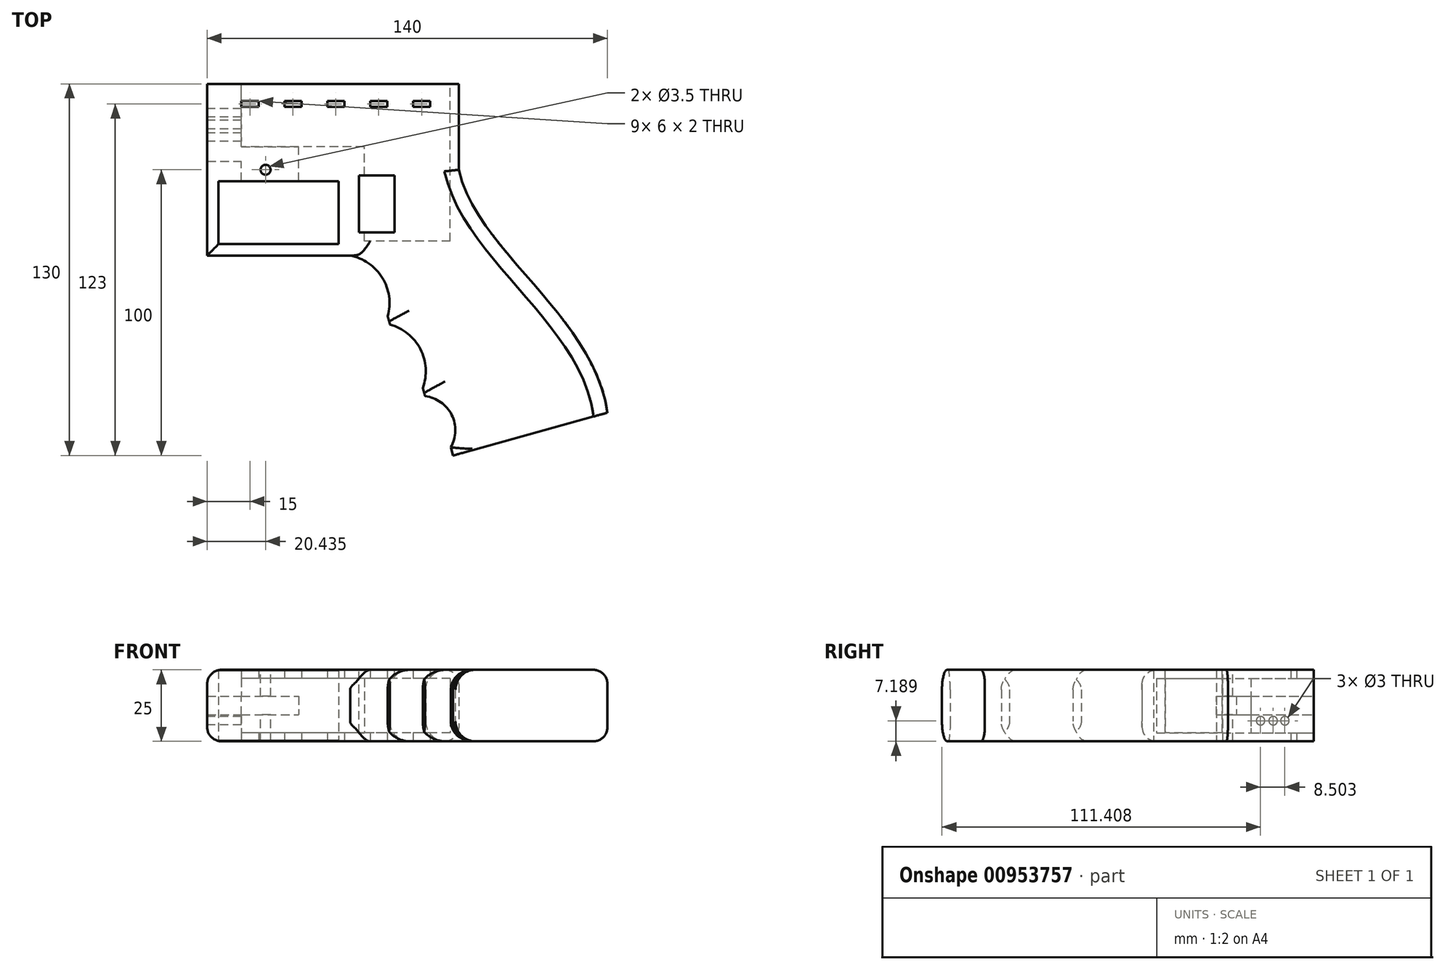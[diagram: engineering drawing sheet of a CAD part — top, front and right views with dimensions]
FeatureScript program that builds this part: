
annotation { "Feature Type Name" : "Feature", "Feature Type Description" : "" }
export const myFeature = defineFeature(function(context is Context, id is Id, definition is map)
    precondition{}
    {
        {
            var Q0;
            Q0=qCreatedBy(makeId("Top.planeOp"),FACE);
            var sketch = newSketch(context, id + "F0", { "sketchPlane" : qUnion([Q0])});
            skLineSegment(sketch, "E0.bottom", {"start": v(-44, 30) * mm, "end": v(44, 30) * mm});
            skLineSegment(sketch, "E0.top", {"start": v(-44, -30) * mm, "end": v(44, -30) * mm});
            skLineSegment(sketch, "E0.left", {"start": v(-44, 30) * mm, "end": v(-44, -30) * mm});
            skLineSegment(sketch, "E0.right", {"start": v(44, 30) * mm, "end": v(44, -30) * mm});
            skPoint(sketch, "E0.middle", {"position": v(0, 0) * mm});
            skLineSegment(sketch, "E1.bottom", {"start": v(-40, -4) * mm, "end": v(2, -4) * mm});
            skLineSegment(sketch, "E1.top", {"start": v(-40, -26) * mm, "end": v(2, -26) * mm});
            skLineSegment(sketch, "E1.left", {"start": v(-40, -4) * mm, "end": v(-40, -26) * mm});
            skLineSegment(sketch, "E1.right", {"start": v(2, -4) * mm, "end": v(2, -26) * mm});
            skLineSegment(sketch, "E2.bottom", {"start": v(-32, 24) * mm, "end": v(-26, 24) * mm});
            skLineSegment(sketch, "E2.top", {"start": v(-32, 22) * mm, "end": v(-26, 22) * mm});
            skLineSegment(sketch, "E2.left", {"start": v(-32, 24) * mm, "end": v(-32, 22) * mm});
            skLineSegment(sketch, "E2.right", {"start": v(-26, 24) * mm, "end": v(-26, 22) * mm});
            skLineSegment(sketch, "E3.1.0.0", {"start": v(-17, 24) * mm, "end": v(-11, 24) * mm});
            skLineSegment(sketch, "E3.1.0.1", {"start": v(-17, 22) * mm, "end": v(-11, 22) * mm});
            skLineSegment(sketch, "E3.1.0.2", {"start": v(-11, 24) * mm, "end": v(-11, 22) * mm});
            skLineSegment(sketch, "E3.1.0.3", {"start": v(-17, 24) * mm, "end": v(-17, 22) * mm});
            skLineSegment(sketch, "E3.2.0.0", {"start": v(-2, 24) * mm, "end": v(4, 24) * mm});
            skLineSegment(sketch, "E3.2.0.1", {"start": v(-2, 22) * mm, "end": v(4, 22) * mm});
            skLineSegment(sketch, "E3.2.0.2", {"start": v(4, 24) * mm, "end": v(4, 22) * mm});
            skLineSegment(sketch, "E3.2.0.3", {"start": v(-2, 24) * mm, "end": v(-2, 22) * mm});
            skLineSegment(sketch, "E3.direction1", {"start": v(-32, 22) * mm, "end": v(-17, 22) * mm, "construction": true});
            skLineSegment(sketch, "E4.0.3.0", {"start": v(13, 24) * mm, "end": v(19, 24) * mm});
            skLineSegment(sketch, "E4.3.3.0", {"start": v(13, 22) * mm, "end": v(19, 22) * mm});
            skLineSegment(sketch, "E4.6.3.0", {"start": v(19, 24) * mm, "end": v(19, 22) * mm});
            skLineSegment(sketch, "E4.9.3.0", {"start": v(13, 24) * mm, "end": v(13, 22) * mm});
            skLineSegment(sketch, "E4.0.4.0", {"start": v(28, 24) * mm, "end": v(34, 24) * mm});
            skLineSegment(sketch, "E4.3.4.0", {"start": v(28, 22) * mm, "end": v(34, 22) * mm});
            skLineSegment(sketch, "E4.6.4.0", {"start": v(34, 24) * mm, "end": v(34, 22) * mm});
            skLineSegment(sketch, "E4.9.4.0", {"start": v(28, 24) * mm, "end": v(28, 22) * mm});
            skFitSpline(sketch, "E5", {"points": [v(44, 0) * mm, v(96, -85) * mm], "startDerivative": vector(19.3, -85.84) * mm, "endDerivative": vector(14.65, -101.93) * mm});
            skLineSegment(sketch, "E6", {"start": v(96, -85) * mm, "end": v(42.05, -100) * mm});
            skLineSegment(sketch, "E7", {"start": v(42.05, -100) * mm, "end": v(41.24, -97.1) * mm});
            skArc(sketch, "E8", {"start": v(41.24, -97.1) * mm, "mid": v(41.53, -85.76) * mm, "end": v(32.23, -79.26) * mm});
            skLineSegment(sketch, "E9", {"start": v(32.23, -79.26) * mm, "end": v(31.42, -76.37) * mm});
            skArc(sketch, "E10", {"start": v(31.42, -76.37) * mm, "mid": v(30.55, -62.75) * mm, "end": v(19.95, -54.16) * mm});
            skLineSegment(sketch, "E11", {"start": v(19.95, -54.16) * mm, "end": v(19.14, -51.27) * mm});
            skArc(sketch, "E12", {"start": v(19.14, -51.27) * mm, "mid": v(17.23, -37.75) * mm, "end": v(6, -30) * mm});
            skSolve(sketch);
        }
        {
            var Q0;
            {var subQ5=sQuery(id+"F0.wireOp",EDGE,"E0.bottom");Q0=makeQuery(id+"F0.imprint","IMPRINT",FACE,{"disambiguationData":[TD([[makeQuery(id+"F0.imprint","IMPRINT",EDGE,{"derivedFrom":subQ5}),-1.0]])]});}
            var Q1;
            {var subQ0=sQuery(id+"F0.wireOp",EDGE,"E5");Q1=makeQuery(id+"F0.imprint","IMPRINT",FACE,{"disambiguationData":[TD([[makeQuery(id+"F0.imprint","IMPRINT",EDGE,{"derivedFrom":subQ0}),-1.0]])]});}
            extrude(context, id + "F1", {"entities" : qUnion([Q0, Q1]), "depth" : 25 * mm, "offsetDistance" : 25 * mm});
        }
        {
            var Q0;
            Q0=makeQuery(id+"F1.opExtrude","SWEPT_FACE",FACE,{"disambiguationData":[OSD([sQuery(id+"F0.wireOp",EDGE,"E0.bottom")])]});
            var sketch = newSketch(context, id + "F2", { "sketchPlane" : qUnion([Q0])});
            skLineSegment(sketch, "E13.bottom", {"start": v(-41, 22) * mm, "end": v(32, 22) * mm});
            skLineSegment(sketch, "E13.top", {"start": v(-41, 3) * mm, "end": v(32, 3) * mm});
            skLineSegment(sketch, "E13.left", {"start": v(-41, 22) * mm, "end": v(-41, 3) * mm});
            skLineSegment(sketch, "E13.right", {"start": v(32, 22) * mm, "end": v(32, 3) * mm});
            skLineSegment(sketch, "E14", {"start": v(-11, 22) * mm, "end": v(-11, 3) * mm});
            skLineSegment(sketch, "E15.bottom", {"start": v(44, 15.75) * mm, "end": v(12, 15.75) * mm});
            skLineSegment(sketch, "E15.top", {"start": v(44, 9.25) * mm, "end": v(12, 9.25) * mm});
            skLineSegment(sketch, "E15.left", {"start": v(44, 15.75) * mm, "end": v(44, 9.25) * mm});
            skLineSegment(sketch, "E15.right", {"start": v(12, 15.75) * mm, "end": v(12, 9.25) * mm});
            skLineSegment(sketch, "E16", {"start": v(25.85, 15.75) * mm, "end": v(25.85, 22) * mm, "construction": true});
            skLineSegment(sketch, "E17", {"start": v(25.61, 9.25) * mm, "end": v(25.61, 3) * mm, "construction": true});
            skSolve(sketch);
        }
        {
            var Q0;
            {var subQ0=sQuery(id+"F2.wireOp",EDGE,"E13.left");Q0=makeQuery(id+"F2.imprint","IMPRINT",FACE,{"disambiguationData":[TD([[makeQuery(id+"F2.imprint","IMPRINT",EDGE,{"derivedFrom":subQ0}),1.0]])]});}
            var Q1;
            {var subQ9=sQuery(id+"F2.wireOp",EDGE,"E14");Q1=makeQuery(id+"F2.imprint","IMPRINT",FACE,{"disambiguationData":[TD([[makeQuery(id+"F2.imprint","IMPRINT",EDGE,{"derivedFrom":subQ9}),1.0]])]});}
            var Q2;
            {var subQ5=sQuery(id+"F2.wireOp",EDGE,"E15.right");Q2=makeQuery(id+"F2.imprint","IMPRINT",FACE,{"disambiguationData":[TD([[makeQuery(id+"F2.imprint","IMPRINT",EDGE,{"derivedFrom":subQ5}),1.0]])]});}
            var Q3;
            {var subQ5=sQuery(id+"F2.wireOp",EDGE,"E15.left");Q3=makeQuery(id+"F2.imprint","IMPRINT",FACE,{"disambiguationData":[TD([[makeQuery(id+"F2.imprint","IMPRINT",EDGE,{"derivedFrom":subQ5}),-1.0]])]});}
            extrude(context, id + "F3", {"entities" : qUnion([Q0, Q1, Q2, Q3]), "operationType" : NewBodyOperationType.REMOVE, "oppositeDirection" : true, "depth" : 22 * mm, "offsetDistance" : 25 * mm});
        }
        {
            var Q0;
            {var subQ0=sQuery(id+"F2.wireOp",EDGE,"E13.left");Q0=makeQuery(id+"F2.imprint","IMPRINT",FACE,{"disambiguationData":[TD([[makeQuery(id+"F2.imprint","IMPRINT",EDGE,{"derivedFrom":subQ0}),1.0]])]});}
            extrude(context, id + "F4", {"entities" : qUnion([Q0]), "operationType" : NewBodyOperationType.REMOVE, "oppositeDirection" : true, "depth" : 55 * mm, "offsetDistance" : 25 * mm});
        }
        {
            var Q0;
            {var subQ5=sQuery(id+"F2.wireOp",EDGE,"E15.right");Q0=makeQuery(id+"F2.imprint","IMPRINT",FACE,{"disambiguationData":[TD([[makeQuery(id+"F2.imprint","IMPRINT",EDGE,{"derivedFrom":subQ5}),1.0]])]});}
            var Q1;
            Q1=makeQuery(id+"F1.opExtrude","SWEPT_FACE",FACE,{"disambiguationData":[OSD([sQuery(id+"F0.wireOp",EDGE,"E1.bottom")])]});
            extrude(context, id + "F5", {"entities" : qUnion([Q0]), "operationType" : NewBodyOperationType.REMOVE, "endBound" : BoundingType.UP_TO_SURFACE, "oppositeDirection" : true, "depth" : 25 * mm, "endBoundEntityFace" : qUnion([Q1]), "offsetDistance" : 25 * mm});
        }
        {
            var Q0;
            {var subQ5=sQuery(id+"F2.wireOp",EDGE,"E15.left");Q0=makeQuery(id+"F2.imprint","IMPRINT",FACE,{"disambiguationData":[TD([[makeQuery(id+"F2.imprint","IMPRINT",EDGE,{"derivedFrom":subQ5}),-1.0]])]});}
            extrude(context, id + "F6", {"entities" : qUnion([Q0]), "operationType" : NewBodyOperationType.REMOVE, "oppositeDirection" : true, "depth" : 27 * mm, "offsetDistance" : 25 * mm});
        }
        {
            var Q0;
            Q0=makeQuery(id+"F1.opExtrude","CAP_EDGE",EDGE,{"disambiguationData":[OSD([sQuery(id+"F0.wireOp",EDGE,"E11")])],"isStart":false});
            var Q1;
            Q1=makeQuery(id+"F1.opExtrude","CAP_EDGE",EDGE,{"disambiguationData":[OSD([sQuery(id+"F0.wireOp",EDGE,"E12")])],"isStart":false});
            var Q2;
            Q2=makeQuery(id+"F1.opExtrude","CAP_EDGE",EDGE,{"disambiguationData":[OSD([sQuery(id+"F0.wireOp",EDGE,"E10")])],"isStart":false});
            var Q3;
            Q3=makeQuery(id+"F1.opExtrude","CAP_EDGE",EDGE,{"disambiguationData":[OSD([sQuery(id+"F0.wireOp",EDGE,"E9")])],"isStart":false});
            var Q4;
            Q4=makeQuery(id+"F1.opExtrude","CAP_EDGE",EDGE,{"disambiguationData":[OSD([sQuery(id+"F0.wireOp",EDGE,"E8")])],"isStart":false});
            var Q5;
            Q5=makeQuery(id+"F1.opExtrude","CAP_EDGE",EDGE,{"disambiguationData":[OSD([sQuery(id+"F0.wireOp",EDGE,"E7")])],"isStart":false});
            fillet(context, id + "F7", {"entities" : qUnion([Q0, Q1, Q2, Q3, Q4, Q5]), "radius" : 7 * mm, "tangentPropagation" : true, "allowEdgeOverflow" : false});
        }
        {
            var Q0;
            Q0=makeQuery(id+"F1.opExtrude","CAP_EDGE",EDGE,{"disambiguationData":[OSD([sQuery(id+"F0.wireOp",EDGE,"E12")])],"isStart":true});
            var Q1;
            Q1=makeQuery(id+"F1.opExtrude","CAP_EDGE",EDGE,{"disambiguationData":[OSD([sQuery(id+"F0.wireOp",EDGE,"E11")])],"isStart":true});
            var Q2;
            Q2=makeQuery(id+"F1.opExtrude","CAP_EDGE",EDGE,{"disambiguationData":[OSD([sQuery(id+"F0.wireOp",EDGE,"E10")])],"isStart":true});
            var Q3;
            Q3=makeQuery(id+"F1.opExtrude","CAP_EDGE",EDGE,{"disambiguationData":[OSD([sQuery(id+"F0.wireOp",EDGE,"E9")])],"isStart":true});
            var Q4;
            Q4=makeQuery(id+"F1.opExtrude","CAP_EDGE",EDGE,{"disambiguationData":[OSD([sQuery(id+"F0.wireOp",EDGE,"E8")])],"isStart":true});
            var Q5;
            Q5=makeQuery(id+"F1.opExtrude","CAP_EDGE",EDGE,{"disambiguationData":[OSD([sQuery(id+"F0.wireOp",EDGE,"E7")])],"isStart":true});
            fillet(context, id + "F8", {"entities" : qUnion([Q0, Q1, Q2, Q3, Q4, Q5]), "radius" : 7 * mm, "tangentPropagation" : true, "allowEdgeOverflow" : false});
        }
        {
            var Q0;
            Q0=makeQuery(id+"F1.opExtrude","CAP_EDGE",EDGE,{"disambiguationData":[OSD([sQuery(id+"F0.wireOp",EDGE,"E0.left")])],"isStart":false});
            var Q1;
            Q1=makeQuery(id+"F1.opExtrude","CAP_EDGE",EDGE,{"disambiguationData":[OSD([sQuery(id+"F0.wireOp",EDGE,"E0.top")])],"isStart":false});
            var Q2;
            Q2=makeQuery(id+"F1.opExtrude","CAP_EDGE",EDGE,{"disambiguationData":[OSD([sQuery(id+"F0.wireOp",EDGE,"E0.right")])],"isStart":false});
            var Q3;
            Q3=makeQuery(id+"F1.opExtrude","CAP_EDGE",EDGE,{"disambiguationData":[OSD([sQuery(id+"F0.wireOp",EDGE,"E5")])],"isStart":false});
            var Q4;
            Q4=makeQuery(id+"F1.opExtrude","CAP_EDGE",EDGE,{"disambiguationData":[OSD([sQuery(id+"F0.wireOp",EDGE,"E5")])],"isStart":true});
            var Q5;
            Q5=makeQuery(id+"F1.opExtrude","CAP_EDGE",EDGE,{"disambiguationData":[OSD([sQuery(id+"F0.wireOp",EDGE,"E0.right")])],"isStart":true});
            var Q6;
            Q6=makeQuery(id+"F1.opExtrude","CAP_EDGE",EDGE,{"disambiguationData":[OSD([sQuery(id+"F0.wireOp",EDGE,"E0.left")])],"isStart":true});
            var Q7;
            Q7=makeQuery(id+"F1.opExtrude","CAP_EDGE",EDGE,{"disambiguationData":[OSD([sQuery(id+"F0.wireOp",EDGE,"E0.top")])],"isStart":true});
            fillet(context, id + "F9", {"entities" : qUnion([Q0, Q1, Q2, Q3, Q4, Q5, Q6, Q7]), "radius" : 5 * mm, "tangentPropagation" : true, "allowEdgeOverflow" : false});
        }
        {
            var Q0;
            Q0=makeQuery(id+"F1.opExtrude","CAP_FACE",FACE,{"disambiguationData":[OSD([sQuery(id+"F0.wireOp",EDGE,"E0.bottom"),sQuery(id+"F0.wireOp",EDGE,"E0.top"),sQuery(id+"F0.wireOp",EDGE,"E0.left"),sQuery(id+"F0.wireOp",EDGE,"E0.right"),sQuery(id+"F0.wireOp",EDGE,"E1.bottom"),sQuery(id+"F0.wireOp",EDGE,"E1.top"),sQuery(id+"F0.wireOp",EDGE,"E1.left"),sQuery(id+"F0.wireOp",EDGE,"E1.right"),sQuery(id+"F0.wireOp",EDGE,"E2.bottom"),sQuery(id+"F0.wireOp",EDGE,"E2.top"),sQuery(id+"F0.wireOp",EDGE,"E2.left"),sQuery(id+"F0.wireOp",EDGE,"E2.right"),sQuery(id+"F0.wireOp",EDGE,"E3.1.0.0"),sQuery(id+"F0.wireOp",EDGE,"E3.1.0.1"),sQuery(id+"F0.wireOp",EDGE,"E3.1.0.2"),sQuery(id+"F0.wireOp",EDGE,"E3.1.0.3"),sQuery(id+"F0.wireOp",EDGE,"E3.2.0.0"),sQuery(id+"F0.wireOp",EDGE,"E3.2.0.1"),sQuery(id+"F0.wireOp",EDGE,"E3.2.0.2"),sQuery(id+"F0.wireOp",EDGE,"E3.2.0.3"),sQuery(id+"F0.wireOp",EDGE,"E4.0.3.0"),sQuery(id+"F0.wireOp",EDGE,"E4.3.3.0"),sQuery(id+"F0.wireOp",EDGE,"E4.6.3.0"),sQuery(id+"F0.wireOp",EDGE,"E4.9.3.0"),sQuery(id+"F0.wireOp",EDGE,"E4.0.4.0"),sQuery(id+"F0.wireOp",EDGE,"E4.3.4.0"),sQuery(id+"F0.wireOp",EDGE,"E4.6.4.0"),sQuery(id+"F0.wireOp",EDGE,"E4.9.4.0"),sQuery(id+"F0.wireOp",EDGE,"E5"),sQuery(id+"F0.wireOp",EDGE,"E6"),sQuery(id+"F0.wireOp",EDGE,"E7"),sQuery(id+"F0.wireOp",EDGE,"E8"),sQuery(id+"F0.wireOp",EDGE,"E9"),sQuery(id+"F0.wireOp",EDGE,"E10"),sQuery(id+"F0.wireOp",EDGE,"E11"),sQuery(id+"F0.wireOp",EDGE,"E12")])],"isStart":false});
            var sketch = newSketch(context, id + "F10", { "sketchPlane" : qUnion([Q0])});
            skCircle(sketch, "E18", {"center": v(-23.57, 0) * mm, "radius": 1.75 * mm});
            skSolve(sketch);
        }
        {
            var Q0;
            Q0=makeQuery(id+"F10.imprint","IMPRINT",FACE,{"disambiguationData":[TD([[makeQuery(id+"F10.imprint","IMPRINT",EDGE,{"derivedFrom":sQuery(id+"F10.wireOp",EDGE,"E18")}),1.0]])]});
            extrude(context, id + "F11", {"entities" : qUnion([Q0]), "operationType" : NewBodyOperationType.REMOVE, "endBound" : BoundingType.THROUGH_ALL, "oppositeDirection" : true, "depth" : 25 * mm, "offsetDistance" : 25 * mm});
        }
        {
            var Q0;
            Q0=makeQuery(id+"F1.opExtrude","SWEPT_FACE",FACE,{"disambiguationData":[OSD([sQuery(id+"F0.wireOp",EDGE,"E0.left")])]});
            var sketch = newSketch(context, id + "F12", { "sketchPlane" : qUnion([Q0])});
            skCircle(sketch, "E19", {"center": v(-19.91, 7.19) * mm, "radius": 1.5 * mm});
            skCircle(sketch, "E20", {"center": v(-15.82, 7.19) * mm, "radius": 1.5 * mm});
            skCircle(sketch, "E21", {"center": v(-11.4, 7.19) * mm, "radius": 1.5 * mm});
            skSolve(sketch);
        }
        {
            var Q0;
            Q0 = qSketchRegion(id + "F12", true);
            extrude(context, id + "F13", {"entities" : qUnion([Q0]), "operationType" : NewBodyOperationType.REMOVE, "endBound" : BoundingType.UP_TO_NEXT, "oppositeDirection" : true, "depth" : 25 * mm, "offsetDistance" : 25 * mm});
        }
        {
            var Q0;
            Q0=makeQuery(id+"F10.imprint","IMPRINT",FACE,{"disambiguationData":[TD([[makeQuery(id+"F10.imprint","IMPRINT",EDGE,{"derivedFrom":sQuery(id+"F10.wireOp",EDGE,"E18")}),-1.0]])]});
            var Q1;
            Q1=makeQuery(id+"F10.imprint","IMPRINT",FACE,{"disambiguationData":[TD([[makeQuery(id+"F10.imprint","IMPRINT",EDGE,{"derivedFrom":sQuery(id+"F10.wireOp",EDGE,"E18")}),-1.0]])]});
            var sketch = newSketch(context, id + "F14", { "sketchPlane" : qUnion([Q0, Q1])});
            skLineSegment(sketch, "E22.bottom", {"start": v(9.09, -1.98) * mm, "end": v(21.59, -1.98) * mm});
            skLineSegment(sketch, "E22.top", {"start": v(9.09, -21.98) * mm, "end": v(21.59, -21.98) * mm});
            skLineSegment(sketch, "E22.left", {"start": v(9.09, -1.98) * mm, "end": v(9.09, -21.98) * mm});
            skLineSegment(sketch, "E22.right", {"start": v(21.59, -1.98) * mm, "end": v(21.59, -21.98) * mm});
            skSolve(sketch);
        }
        {
            var Q0;
            Q0 = qSketchRegion(id + "F14", true);
            var Q1;
            {var subQ0=sQuery(id+"F2.wireOp",EDGE,"E13.top");Q1=makeQuery(id+"F4.boolean.opBoolean","MERGE",FACE,{"derivedFrom":[makeQuery(id+"F3.boolean.opBoolean","COPY",FACE,{"derivedFrom":makeQuery(id+"F3.opExtrude","SWEPT_FACE",FACE,{"disambiguationData":[OSD([subQ0])]})})],"fromTools":[makeQuery(id+"F4.opExtrude","SWEPT_FACE",FACE,{"disambiguationData":[OSD([subQ0])]})]});}
            extrude(context, id + "F15", {"entities" : qUnion([Q0]), "operationType" : NewBodyOperationType.REMOVE, "endBound" : BoundingType.UP_TO_SURFACE, "oppositeDirection" : true, "depth" : 25 * mm, "endBoundEntityFace" : qUnion([Q1]), "offsetDistance" : 25 * mm});
        }
    });
